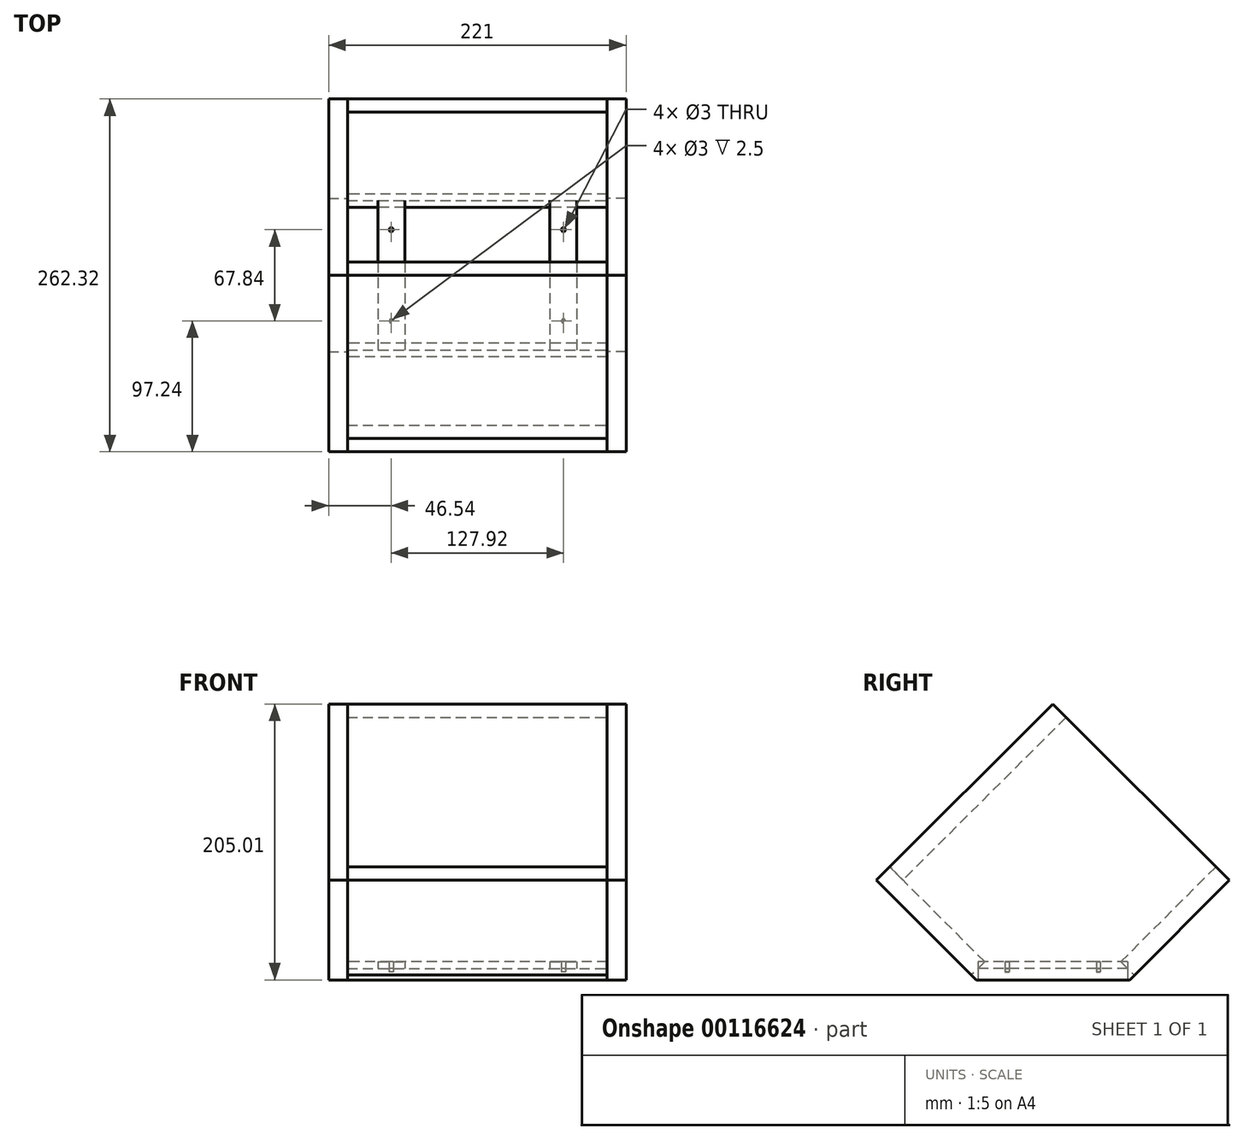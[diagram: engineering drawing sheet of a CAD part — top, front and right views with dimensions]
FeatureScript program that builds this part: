
annotation { "Feature Type Name" : "Feature", "Feature Type Description" : "" }
export const myFeature = defineFeature(function(context is Context, id is Id, definition is map)
    precondition{}
    {
        {
            var Q0;
            Q0=qCreatedBy(makeId("Top.planeOp"),FACE);
            var sketch = newSketch(context, id + "F0", { "sketchPlane" : qUnion([Q0])});
            skLineSegment(sketch, "E0.bottom", {"start": v(-96.5, 55.5) * mm, "end": v(96.5, 55.5) * mm});
            skLineSegment(sketch, "E0.top", {"start": v(-96.5, -55.5) * mm, "end": v(96.5, -55.5) * mm});
            skLineSegment(sketch, "E0.left", {"start": v(-96.5, 55.5) * mm, "end": v(-96.5, -55.5) * mm});
            skLineSegment(sketch, "E0.right", {"start": v(96.5, 55.5) * mm, "end": v(96.5, -55.5) * mm});
            skSolve(sketch);
        }
        {
            var Q0;
            Q0 = qSketchRegion(id + "F0", true);
            extrude(context, id + "F1", {"entities" : qUnion([Q0]), "depth" : 8.5 * mm});
        }
        {
            var Q0;
            Q0=makeQuery(id+"F1.opExtrude","CAP_FACE",FACE,{"disambiguationData":[OSD([sQuery(id+"F0.wireOp",EDGE,"E0.bottom"),sQuery(id+"F0.wireOp",EDGE,"E0.top"),sQuery(id+"F0.wireOp",EDGE,"E0.left"),sQuery(id+"F0.wireOp",EDGE,"E0.right")])],"isStart":false});
            var sketch = newSketch(context, id + "F2", { "sketchPlane" : qUnion([Q0])});
            skLineSegment(sketch, "E1.bottom", {"start": v(-73.96, 55.5) * mm, "end": v(-53.96, 55.5) * mm});
            skLineSegment(sketch, "E1.top", {"start": v(-73.96, -55.5) * mm, "end": v(-53.96, -55.5) * mm});
            skLineSegment(sketch, "E1.left", {"start": v(-73.96, 55.5) * mm, "end": v(-73.96, -55.5) * mm});
            skLineSegment(sketch, "E1.right", {"start": v(-53.96, 55.5) * mm, "end": v(-53.96, -55.5) * mm});
            skLineSegment(sketch, "E2.bottom", {"start": v(53.96, 55.5) * mm, "end": v(73.96, 55.5) * mm});
            skLineSegment(sketch, "E2.top", {"start": v(53.96, -55.5) * mm, "end": v(73.96, -55.5) * mm});
            skLineSegment(sketch, "E2.left", {"start": v(53.96, 55.5) * mm, "end": v(53.96, -55.5) * mm});
            skLineSegment(sketch, "E2.right", {"start": v(73.96, 55.5) * mm, "end": v(73.96, -55.5) * mm});
            skSolve(sketch);
        }
        {
            var Q0;
            Q0 = qSketchRegion(id + "F2", true);
            extrude(context, id + "F3", {"entities" : qUnion([Q0]), "depth" : 5 * mm});
        }
        {
            var Q0;
            Q0=makeQuery(id+"F1.opExtrude","CAP_FACE",FACE,{"disambiguationData":[OSD([sQuery(id+"F0.wireOp",EDGE,"E0.bottom"),sQuery(id+"F0.wireOp",EDGE,"E0.top"),sQuery(id+"F0.wireOp",EDGE,"E0.left"),sQuery(id+"F0.wireOp",EDGE,"E0.right")])],"isStart":false});
            var sketch = newSketch(context, id + "F4", { "sketchPlane" : qUnion([Q0])});
            skCircle(sketch, "E3", {"center": v(-63.96, 33.92) * mm, "radius": 1.5 * mm});
            skCircle(sketch, "E4", {"center": v(63.96, 33.92) * mm, "radius": 1.5 * mm});
            skCircle(sketch, "E5", {"center": v(-63.96, -33.92) * mm, "radius": 1.5 * mm});
            skCircle(sketch, "E6", {"center": v(63.96, -33.92) * mm, "radius": 1.5 * mm});
            skSolve(sketch);
        }
        {
            var Q0;
            Q0 = qSketchRegion(id + "F4", true);
            extrude(context, id + "F5", {"entities" : qUnion([Q0]), "operationType" : NewBodyOperationType.REMOVE, "endBound" : BoundingType.THROUGH_ALL, "depth" : 2.5 * mm, "hasSecondDirection" : true, "secondDirectionOppositeDirection" : true, "secondDirectionDepth" : 2.5 * mm});
        }
        {
            var Q0;
            {var subQ0=sQuery(id+"F0.wireOp",EDGE,"E0.top");Q0=makeQuery(id+"F3.boolean.opBoolean","SPLIT",EDGE,{"disambiguationData":[TD([makeQuery(id+"F3.opExtrude","SWEPT_FACE",FACE,{"disambiguationData":[OSD([sQuery(id+"F2.wireOp",EDGE,"E1.right")])]})])],"derivedFrom":makeQuery(id+"F1.opExtrude","CAP_EDGE",EDGE,{"disambiguationData":[OSD([subQ0])],"isStart":false})});}
            cPlane(context, id + "F6", {"entities" : qUnion([Q0]), "cplaneType" : CPlaneType.LINE_ANGLE, "offset" : 25 * mm, "angle" : 45 * degree, "width" : 150 * mm, "height" : 150 * mm});
        }
        {
            var Q0;
            Q0=qCreatedBy(id+"F6.planeOp",FACE);
            var sketch = newSketch(context, id + "F7", { "sketchPlane" : qUnion([Q0])});
            skLineSegment(sketch, "E7.bottom", {"start": v(-96.5, 45.25) * mm, "end": v(96.5, 45.25) * mm});
            skLineSegment(sketch, "E7.top", {"start": v(-96.5, 145.25) * mm, "end": v(96.5, 145.25) * mm});
            skLineSegment(sketch, "E7.left", {"start": v(-96.5, 45.25) * mm, "end": v(-96.5, 145.25) * mm});
            skLineSegment(sketch, "E7.right", {"start": v(96.5, 45.25) * mm, "end": v(96.5, 145.25) * mm});
            skSolve(sketch);
        }
        {
            var Q0;
            Q0 = qSketchRegion(id + "F7", true);
            extrude(context, id + "F8", {"entities" : qUnion([Q0]), "endBound" : BoundingType.SYMMETRIC, "depth" : 14 * mm});
        }
        {
            var Q0;
            Q0=makeQuery(id+"F8.opExtrude","SWEPT_BODY",BODY,{"disambiguationData":[OSD([sQuery(id+"F7.wireOp",EDGE,"E7.bottom"),sQuery(id+"F7.wireOp",EDGE,"E7.top"),sQuery(id+"F7.wireOp",EDGE,"E7.left"),sQuery(id+"F7.wireOp",EDGE,"E7.right")])]});
            var Q1;
            Q1=qCreatedBy(makeId("Front.planeOp"),FACE);
            mirror(context, id + "F9", {"entities" : qUnion([Q0]), "mirrorPlane" : qUnion([Q1])});
        }
        {
            var Q0;
            Q0=makeQuery(id+"F8.opExtrude","SWEPT_FACE",FACE,{"disambiguationData":[OSD([sQuery(id+"F7.wireOp",EDGE,"E7.right")])]});
            var sketch = newSketch(context, id + "F10", { "sketchPlane" : qUnion([Q0])});
            skLineSegment(sketch, "E8", {"start": v(131.16, 74.26) * mm, "end": v(56.9, 0) * mm});
            skLineSegment(sketch, "E9", {"start": v(-131.16, 74.26) * mm, "end": v(-57.13, 0) * mm});
            skLineSegment(sketch, "E10", {"start": v(-57.13, 0) * mm, "end": v(56.9, 0) * mm});
            skLineSegment(sketch, "E11", {"start": v(-131.16, 74.26) * mm, "end": v(0, 205) * mm});
            skLineSegment(sketch, "E12", {"start": v(0, 205) * mm, "end": v(131.16, 74.26) * mm});
            skSolve(sketch);
        }
        {
            var Q0;
            Q0 = qSketchRegion(id + "F10", true);
            extrude(context, id + "F11", {"entities" : qUnion([Q0]), "depth" : 14 * mm});
        }
        {
            var Q0;
            Q0=makeQuery(id+"F11.opExtrude","SWEPT_BODY",BODY,{"disambiguationData":[OSD([sQuery(id+"F10.wireOp",EDGE,"E8"),sQuery(id+"F10.wireOp",EDGE,"E9"),sQuery(id+"F10.wireOp",EDGE,"E10"),sQuery(id+"F10.wireOp",EDGE,"E11"),sQuery(id+"F10.wireOp",EDGE,"E12")])]});
            var Q1;
            Q1=qCreatedBy(makeId("Right.planeOp"),FACE);
            mirror(context, id + "F12", {"entities" : qUnion([Q0]), "mirrorPlane" : qUnion([Q1])});
        }
        {
            var Q0;
            Q0=makeQuery(id+"F11.opExtrude","SWEPT_FACE",FACE,{"disambiguationData":[OSD([sQuery(id+"F10.wireOp",EDGE,"E12")])]});
            var sketch = newSketch(context, id + "F13", { "sketchPlane" : qUnion([Q0])});
            skLineSegment(sketch, "E13.bottom", {"start": v(-96.5, 144.74) * mm, "end": v(96.5, 144.74) * mm});
            skLineSegment(sketch, "E13.top", {"start": v(-96.5, -26.46) * mm, "end": v(96.5, -26.46) * mm});
            skLineSegment(sketch, "E13.left", {"start": v(-96.5, 144.74) * mm, "end": v(-96.5, -26.46) * mm});
            skLineSegment(sketch, "E13.right", {"start": v(96.5, 144.74) * mm, "end": v(96.5, -26.46) * mm});
            skSolve(sketch);
        }
        {
            var Q0;
            Q0 = qSketchRegion(id + "F13", true);
            extrude(context, id + "F14", {"entities" : qUnion([Q0]), "oppositeDirection" : true, "depth" : 14 * mm});
        }
    });
